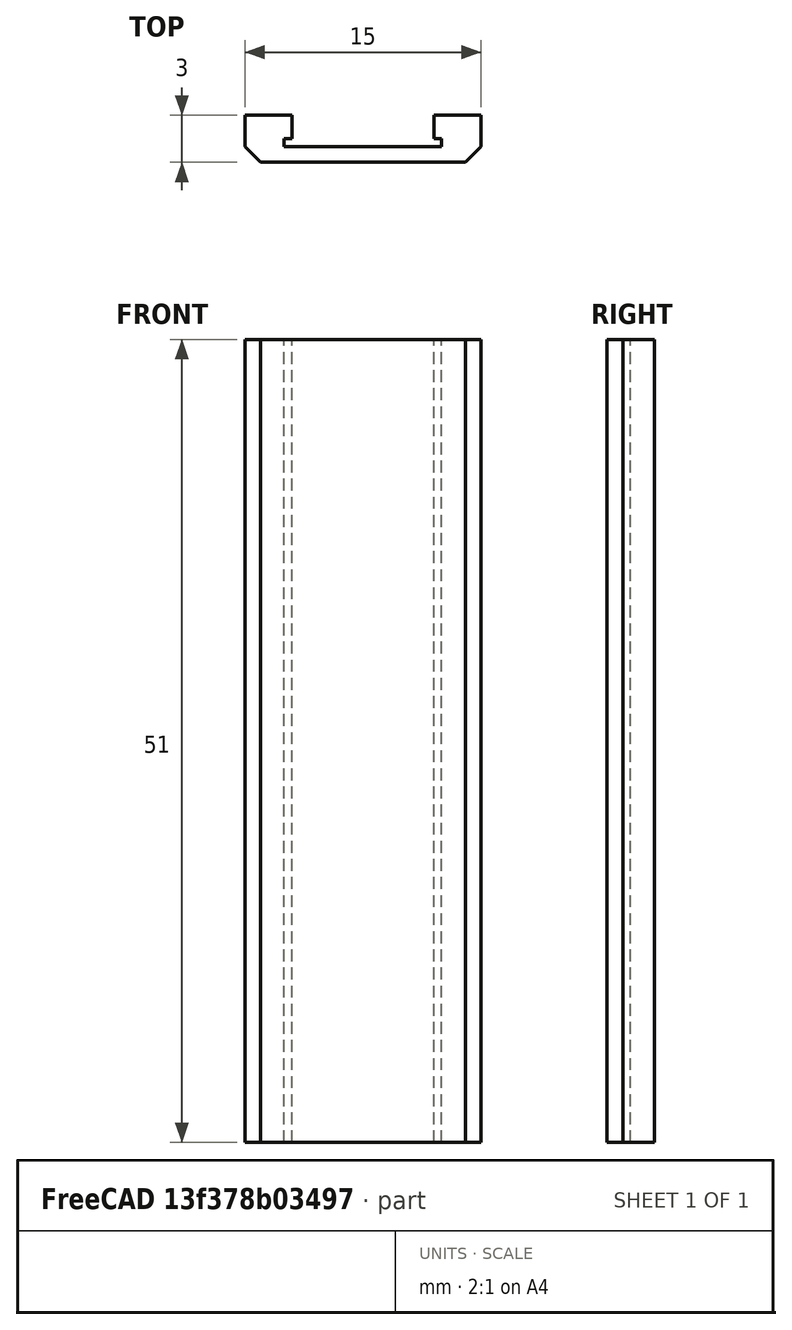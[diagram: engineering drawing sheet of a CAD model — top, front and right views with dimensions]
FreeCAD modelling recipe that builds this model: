
FCSTD DOCUMENT  (FreeCAD 0.20R29603 (Git))
Label: neopixelbracket
License: All rights reserved
LicenseURL: http://en.wikipedia.org/wiki/All_rights_reserved
objects: Sketcher::SketchObject×1, PartDesign::Pad×1, PartDesign::Body×1
note: 4 computed .brp shape members not serialized (recipe doc carries the construction recipe); baked Part::Feature solids carry a one-line shape summary decoded from their .brp

FEATURE [Sketcher::SketchObject] Sketch
  FullyConstrained = true
  MapMode = 5
  Support = -> [XY_Plane]
  sketch-geometry (14):
    g0: LineSegment StartX=-7.5 StartY=3 StartZ=0 EndX=-4.5 EndY=3 EndZ=0
    g1: LineSegment StartX=-4.5 StartY=3 StartZ=0 EndX=-4.5 EndY=1.5 EndZ=0
    g2: LineSegment StartX=-4.5 StartY=1.5 StartZ=0 EndX=-5 EndY=1.5 EndZ=0
    g3: LineSegment StartX=-5 StartY=1.5 StartZ=0 EndX=-5 EndY=1 EndZ=0
    g4: LineSegment StartX=-5 StartY=1 StartZ=0 EndX=5 EndY=1 EndZ=0
    g5: LineSegment StartX=5 StartY=1 StartZ=0 EndX=5 EndY=1.5 EndZ=0
    g6: LineSegment StartX=5 StartY=1.5 StartZ=0 EndX=4.5 EndY=1.5 EndZ=0
    g7: LineSegment StartX=4.5 StartY=1.5 StartZ=0 EndX=4.5 EndY=3 EndZ=0
    g8: LineSegment StartX=4.5 StartY=3 StartZ=0 EndX=7.5 EndY=3 EndZ=0
    g9: LineSegment StartX=7.5 StartY=3 StartZ=0 EndX=7.5 EndY=1 EndZ=0
    g10: LineSegment StartX=7.5 StartY=1 StartZ=0 EndX=6.5 EndY=0 EndZ=0
    g11: LineSegment StartX=6.5 StartY=0 StartZ=0 EndX=-6.5 EndY=0 EndZ=0
    g12: LineSegment StartX=-6.5 StartY=0 StartZ=0 EndX=-7.5 EndY=1 EndZ=0
    g13: LineSegment StartX=-7.5 StartY=1 StartZ=0 EndX=-7.5 EndY=3 EndZ=0
  constraints (42):
    c: Horizontal(g0)
    c: Coincident(g0,g1)
    c: Coincident(g1,g2)
    c: Coincident(g2,g3)
    c: Coincident(g3,g4)
    c: Horizontal(g4)
    c: Coincident(g4,g5)
    c: Vertical(g5)
    c: Coincident(g5,g6)
    c: Horizontal(g6)
    c: Coincident(g6,g7)
    c: Vertical(g7)
    c: Coincident(g7,g8)
    c: Coincident(g8,g9)
    c: Vertical(g9)
    c: Coincident(g9,g10)
    c: Coincident(g10,g11)
    c: Horizontal(g11)
    c: Coincident(g11,g12)
    c: Coincident(g12,g13)
    c: Coincident(g13,g0)
    c: Horizontal(g8)
    c: Vertical(g13)
    c: Vertical(g3)
    c: Vertical(g1)
    c: Horizontal(g2)
    c: DistanceX(g4,g4) = 10
    c: DistanceY(g3,g3) = 0.5
    c: DistanceY(g5,g5) = 0.5
    c: DistanceY(g7,g7) = 1.5
    c: DistanceY(g1,g1) = 1.5
    c: DistanceX(g2,g2) = 0.5
    c: DistanceX(g6,g6) = 0.5
    c: DistanceX(g0,g0) = 3
    c: DistanceX(g8,g8) = 3
    c: DistanceY(g10,g8) = 3
    c: DistanceY(g13,g13) = 2
    c: DistanceY(g9,g9) = 2
    c: DistanceX(g12,g11) = 1
    c: DistanceX(g10,g9) = 1
    c: DistanceY(g-1,g10) = 0
    c: DistanceX(g-1,g4) = 5
FEATURE [PartDesign::Pad] Pad
  Direction = (0,0,1)
  Length = 51
  Length2 = 10
  Profile = -> Sketch
  ReferenceAxis = -> Sketch [N_Axis]
  Type = 0
FEATURE [PartDesign::Body] Body
  Group = -> [Sketch,Pad]
  Origin = -> Origin
  Tip = -> Pad
